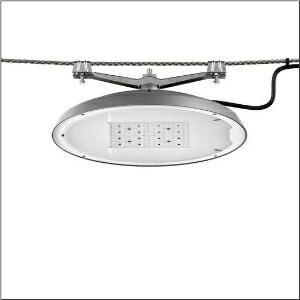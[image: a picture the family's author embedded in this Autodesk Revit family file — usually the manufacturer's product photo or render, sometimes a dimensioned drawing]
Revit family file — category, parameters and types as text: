
# Revit family: dl_r__50_iq_mini___st1_0s_5xa248w41f08me_9ef6
name_source: partatom
category: Lighting Fixtures
units: mm (PartAtom-declared; Revit-internal decimal feet)

## family parameters
Cut with Voids When Loaded = No
Host = Face
Light Source = No
Part Type = Normal
Room Calculation Point = No
Round Connector Dimension = Use Diameter
Shared = No

## types (1)
- --- (1 x LED, 15660 lm, 101.7 W, 4000K)
    Apparent Load = 102 VA
    CIE Flux Codes = 37 72 97 100 100
    Color Rendering = 70
    Color Temperature = 4000K
    Default Elevation = 1800 mm
    Description = DL® 50 iQ mini, catenary luminaire, primary light control with lens, of PMMA, primary optical cover: cover, of toughened safety glass, transparent, light distribution: ST1.0s, light emission: direct distribution, primary light characteristic: symmetric, installation type: suspended mounting, LED, High Power LED, rated luminous flux: 15.660lm, luminous efficacy: 154lm/W, light colour: 740, colour temperature: 4000K, control gear: iQ Street-Remote, control: optimised constant luminous flux control (CLO 2.0), Desk-Remote (wireless, voltage-free reading and setting of iQ features in the workshop via application-optimized NFC function/RFID function), Light-Fading, Smart-Wire, Night-Set, Lumen-Switch, Temp-Guard, Auto-Match, Street-Remote, mains connection: 230..240V, AC, 50/60Hz, start of lifetime: 102W, end of service life: 111W, reduction: 45W, luminaire housing, of diecast aluminium, powder-coated, Siteco® metallic grey (DB 702S), diameter: 500mm, height: 115mm, mounting height: 4..12m, protection rating (complete): IP66, insulation class (complete): insulation class II (safety insulation), certification: CE, ENEC, ENEC+, VDE, impact resistance: IK08, permissible operating ambient temperature for outdoor applications: -25..+40°C, standard-compliant lighting for roads and squares, packaging unit: 1 piece

Light Distribution: ST1.0s
    Height = 124 mm  [stored 0.406824 ft]
    Lamp = 1 x LED
    Lamp Light Flux = 15660 lm
    Lamp Power = 101.7 W
    Lamp count = 1
    Length = 500 mm
    Luminous efficacy = 154 lm/W
    Manufacturer = Siteco
    ModVariant = No
    Model = 5XA248W41F08ME
    Number of Poles = 1
    OnlyDefault = Yes
    Power Factor = 1
    Product Name = DL® 50 iQ mini | ST1.0s
    Product group = catenary luminaire
    ProductGroupID = 6300
    Protection Class = Protection class II
    Protection Degree = IP 66
    RLX_Detail_Level = 1
    RLX_Emergency_Light_Flux = 0 lm
    RLX_Emergency_Type = 0
    RLX_Emergency_Type_DB = No
    RlxData = <blob elided: 127353 chars, md5=20cadb55>
    Socket = socket
    Standby Power = 0 W
    System Light Flux = 15660 lm
    System Power = 102 W
    Type Comments = factory setting: luminous flux: 100 % | dim-lin: 254 | 534 mA
    Type Image = l_1251783.jpg
    URL = http://relux.com
    VarID = @adj_161853
    Voltage = 0 V
    Weight = 0.00 kg
    Width = 0 mm  [stored 0 ft]

note: [stored X ft] marks values corroborated as IEEE doubles in the binary element streams (Revit-internal decimal feet)

## geometry (parser evidence)
native form markers: Blend x4, Sweep x14
no freeform markers — native parametric forms only
